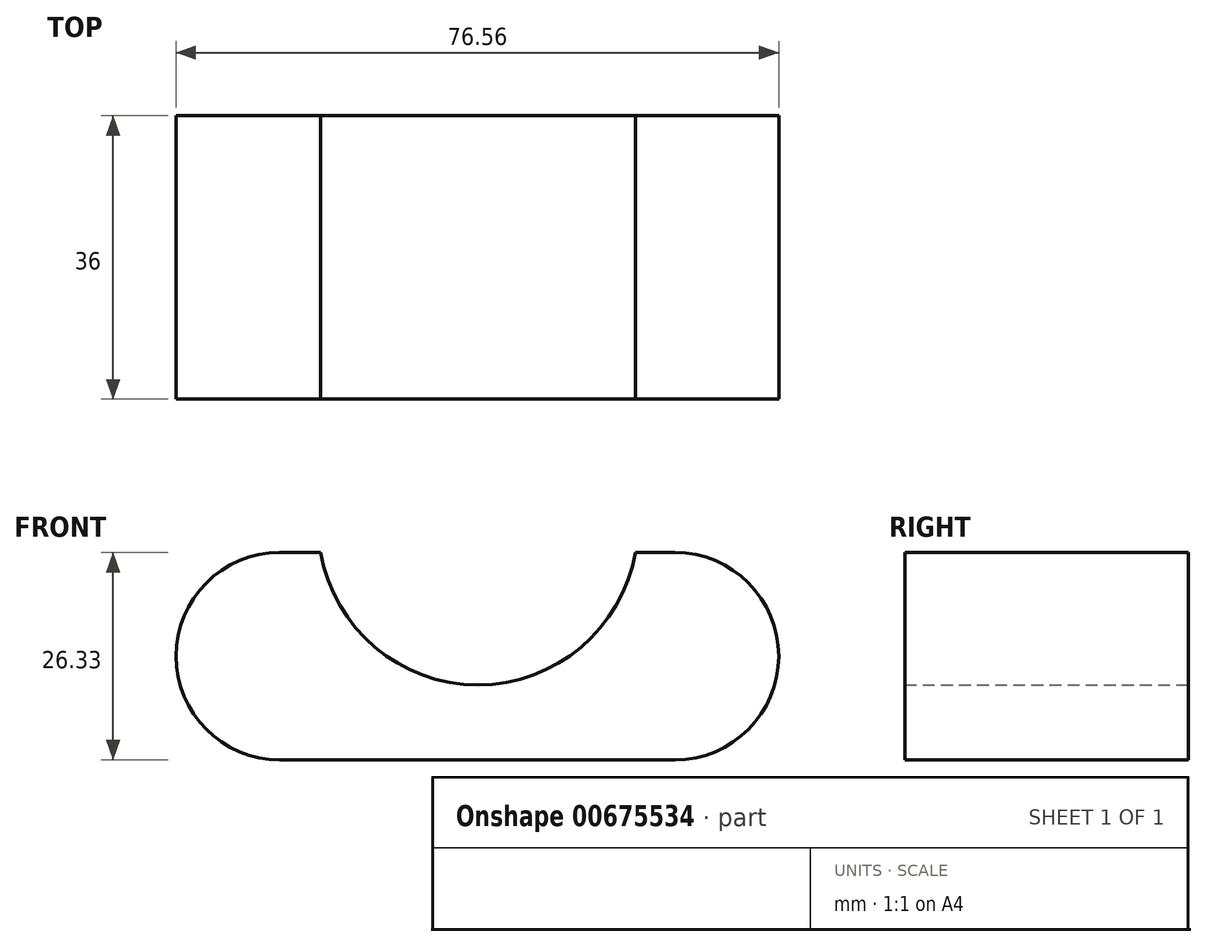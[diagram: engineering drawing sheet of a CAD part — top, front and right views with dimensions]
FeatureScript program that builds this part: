
annotation { "Feature Type Name" : "Feature", "Feature Type Description" : "" }
export const myFeature = defineFeature(function(context is Context, id is Id, definition is map)
    precondition{}
    {
        {
            var Q0;
            Q0=qCreatedBy(makeId("Front.planeOp"),FACE);
            var sketch = newSketch(context, id + "F0", { "sketchPlane" : qUnion([Q0])});
            skLineSegment(sketch, "E0", {"start": v(0, 0) * mm, "end": v(-50.22, 0) * mm});
            skArc(sketch, "E1", {"start": v(-50.22, 26.33) * mm, "mid": v(-63.39, 13.17) * mm, "end": v(-50.22, 0) * mm});
            skArc(sketch, "E2", {"start": v(0, 0) * mm, "mid": v(13.17, 13.17) * mm, "end": v(0, 26.33) * mm});
            skLineSegment(sketch, "E3", {"start": v(-50.22, 26.33) * mm, "end": v(-45.04, 26.33) * mm});
            skLineSegment(sketch, "E4", {"start": v(0, 26.33) * mm, "end": v(-5.04, 26.33) * mm});
            skArc(sketch, "E5", {"start": v(-45.04, 26.33) * mm, "mid": v(-25.04, 9.53) * mm, "end": v(-5.04, 26.33) * mm});
            skSolve(sketch);
        }
        {
            var Q0;
            Q0 = qSketchRegion(id + "F0", true);
            extrude(context, id + "F1", {"entities" : qUnion([Q0]), "depth" : 36 * mm, "offsetDistance" : 25 * mm});
        }
    });
